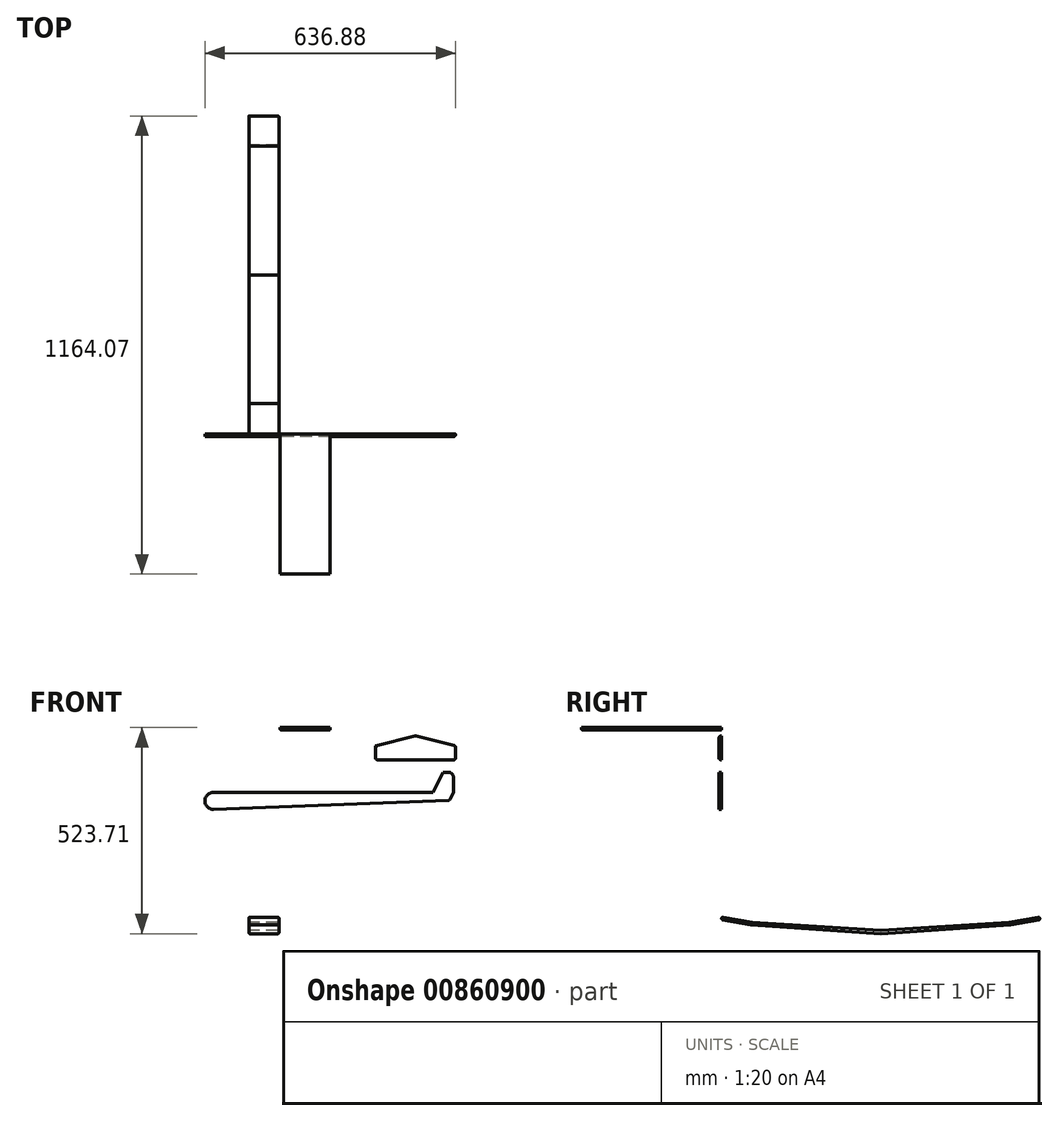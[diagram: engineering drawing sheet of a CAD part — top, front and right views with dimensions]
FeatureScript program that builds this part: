
annotation { "Feature Type Name" : "Feature", "Feature Type Description" : "" }
export const myFeature = defineFeature(function(context is Context, id is Id, definition is map)
    precondition{}
    {
        {
            var Q0;
            Q0=qCreatedBy(makeId("Front.planeOp"),FACE);
            var sketch = newSketch(context, id + "F0", { "sketchPlane" : qUnion([Q0])});
            skLineSegment(sketch, "E0", {"start": v(-90.11, 35.67) * mm, "end": v(445.18, 35.67) * mm});
            skLineSegment(sketch, "E1", {"start": v(493.61, 86.9) * mm, "end": v(506.79, 86.9) * mm});
            skLineSegment(sketch, "E2", {"start": v(519.49, 74.2) * mm, "end": v(519.49, 35.67) * mm});
            skPoint(sketch, "E3.orphan", {"position": v(468.96, 35.67) * mm});
            skLineSegment(sketch, "E4", {"start": v(467.72, 35.67) * mm, "end": v(445.18, 35.67) * mm});
            skLineSegment(sketch, "E5", {"start": v(493.61, 86.9) * mm, "end": v(467.72, 35.67) * mm});
            skPoint(sketch, "E6.visualSharp", {"position": v(519.49, 86.9) * mm});
            skArc(sketch, "E6.filletArc", {"start": v(519.49, 74.2) * mm, "mid": v(515.77, 83.19) * mm, "end": v(506.79, 86.9) * mm});
            skArc(sketch, "E7", {"start": v(-90.11, 35.67) * mm, "mid": v(-111.77, 14.01) * mm, "end": v(-90.11, -7.65) * mm});
            skLineSegment(sketch, "E8", {"start": v(-90.11, -7.65) * mm, "end": v(509.73, 15.45) * mm});
            skLineSegment(sketch, "E9", {"start": v(509.73, 15.45) * mm, "end": v(519.49, 35.67) * mm});
            skSolve(sketch);
        }
        {
            var Q0;
            Q0=qCreatedBy(makeId("Front.planeOp"),FACE);
            var sketch = newSketch(context, id + "F1", { "sketchPlane" : qUnion([Q0])});
            skLineSegment(sketch, "E10", {"start": v(321.9, 118.2) * mm, "end": v(321.9, 153.75) * mm});
            skLineSegment(sketch, "E11", {"start": v(321.9, 153.75) * mm, "end": v(423.5, 179.15) * mm});
            skLineSegment(sketch, "E12", {"start": v(423.5, 179.15) * mm, "end": v(423.5, 118.2) * mm});
            skLineSegment(sketch, "E13", {"start": v(423.5, 118.2) * mm, "end": v(321.9, 118.2) * mm});
            skLineSegment(sketch, "E14.MirrorCS", {"start": v(525.1, 153.75) * mm, "end": v(423.5, 179.15) * mm});
            skLineSegment(sketch, "E15.MirrorCS", {"start": v(423.5, 118.2) * mm, "end": v(525.1, 118.2) * mm});
            skLineSegment(sketch, "E16.MirrorCS", {"start": v(525.1, 118.2) * mm, "end": v(525.1, 153.75) * mm});
            skSolve(sketch);
        }
        {
            var Q0;
            Q0=qCreatedBy(makeId("Front.planeOp"),FACE);
            var sketch = newSketch(context, id + "F2", { "sketchPlane" : qUnion([Q0])});
            skLineSegment(sketch, "E17", {"start": v(79.4, 194.15) * mm, "end": v(206.4, 194.15) * mm});
            skLineSegment(sketch, "E18", {"start": v(206.4, 194.15) * mm, "end": v(206.4, 200.5) * mm});
            skLineSegment(sketch, "E19", {"start": v(206.4, 200.5) * mm, "end": v(79.4, 200.5) * mm});
            skLineSegment(sketch, "E20", {"start": v(79.4, 200.5) * mm, "end": v(79.4, 194.15) * mm});
            skSolve(sketch);
        }
        {
            var Q0;
            Q0=makeQuery(id+"F0.imprint","IMPRINT",FACE,{"disambiguationData":[TD([[makeQuery(id+"F0.imprint","IMPRINT",EDGE,{"derivedFrom":sQuery(id+"F0.wireOp",EDGE,"E0")}),-1.0]])]});
            extrude(context, id + "F3", {"entities" : qUnion([Q0]), "depth" : 6.35 * mm, "offsetDistance" : 25.4 * mm});
        }
        {
            var Q0;
            Q0=makeQuery(id+"F2.imprint","IMPRINT",FACE,{"disambiguationData":[TD([[makeQuery(id+"F2.imprint","IMPRINT",EDGE,{"derivedFrom":sQuery(id+"F2.wireOp",EDGE,"E17")}),1.0]])]});
            extrude(context, id + "F4", {"entities" : qUnion([Q0]), "depth" : 355.6 * mm, "offsetDistance" : 25.4 * mm});
        }
        {
            var Q0;
            Q0=makeQuery(id+"F4.opExtrude","SWEPT_EDGE",EDGE,{"disambiguationData":[OSD([sQuery(id+"F2.wireOp",EDGE,"E17"),sQuery(id+"F2.wireOp",EDGE,"E18")])]});
            var Q1;
            Q1=makeQuery(id+"F4.opExtrude","SWEPT_EDGE",EDGE,{"disambiguationData":[OSD([sQuery(id+"F2.wireOp",EDGE,"E17"),sQuery(id+"F2.wireOp",EDGE,"E20")])]});
            var Q2;
            Q2=makeQuery(id+"F4.opExtrude","CAP_EDGE",EDGE,{"disambiguationData":[OSD([sQuery(id+"F2.wireOp",EDGE,"E17")])],"isStart":false});
            var Q3;
            Q3=makeQuery(id+"F4.opExtrude","CAP_EDGE",EDGE,{"disambiguationData":[OSD([sQuery(id+"F2.wireOp",EDGE,"E17")])],"isStart":true});
            fillet(context, id + "F5", {"entities" : qUnion([Q0, Q1, Q2, Q3]), "radius" : 2.54 * mm, "tangentPropagation" : true, "allowEdgeOverflow" : false});
        }
        {
            var Q0;
            Q0=makeQuery(id+"F1.imprint","IMPRINT",FACE,{"disambiguationData":[TD([[makeQuery(id+"F1.imprint","IMPRINT",EDGE,{"derivedFrom":sQuery(id+"F1.wireOp",EDGE,"E10")}),-1.0]])]});
            var Q1;
            Q1=makeQuery(id+"F1.imprint","IMPRINT",FACE,{"disambiguationData":[TD([[makeQuery(id+"F1.imprint","IMPRINT",EDGE,{"derivedFrom":sQuery(id+"F1.wireOp",EDGE,"E12")}),1.0]])]});
            extrude(context, id + "F6", {"entities" : qUnion([Q0, Q1]), "depth" : 6.35 * mm, "offsetDistance" : 25.4 * mm});
        }
        {
            var Q0;
            Q0=qCreatedBy(makeId("Right.planeOp"),FACE);
            var sketch = newSketch(context, id + "F7", { "sketchPlane" : qUnion([Q0])});
            skLineSegment(sketch, "E21", {"start": v(404.44, -323.21) * mm, "end": v(75, -300.8) * mm});
            skLineSegment(sketch, "E22", {"start": v(75, -300.8) * mm, "end": v(0, -287.34) * mm});
            skLineSegment(sketch, "E23", {"start": v(0, -287.34) * mm, "end": v(1.12, -281.1) * mm});
            skLineSegment(sketch, "E24", {"start": v(1.12, -281.1) * mm, "end": v(77.4, -294.77) * mm});
            skLineSegment(sketch, "E25", {"start": v(77.4, -294.77) * mm, "end": v(404.44, -314.39) * mm});
            skLineSegment(sketch, "E26", {"start": v(404.44, -314.39) * mm, "end": v(404.44, -323.21) * mm});
            skLineSegment(sketch, "E27.MirrorCS", {"start": v(731.49, -294.77) * mm, "end": v(404.44, -314.39) * mm});
            skLineSegment(sketch, "E28.MirrorCS", {"start": v(807.76, -281.1) * mm, "end": v(731.49, -294.77) * mm});
            skLineSegment(sketch, "E29.MirrorCS", {"start": v(808.88, -287.34) * mm, "end": v(807.76, -281.1) * mm});
            skLineSegment(sketch, "E30.MirrorCS", {"start": v(733.88, -300.8) * mm, "end": v(808.88, -287.34) * mm});
            skLineSegment(sketch, "E31.MirrorCS", {"start": v(404.44, -323.21) * mm, "end": v(733.88, -300.8) * mm});
            skSolve(sketch);
        }
        {
            var Q0;
            Q0 = qSketchRegion(id + "F7", true);
            extrude(context, id + "F8", {"entities" : qUnion([Q0]), "depth" : 76.2 * mm, "offsetDistance" : 25.4 * mm});
        }
        {
            var Q0;
            Q0=makeQuery(id+"F8.opExtrude","SWEPT_EDGE",EDGE,{"disambiguationData":[OSD([sQuery(id+"F7.wireOp",EDGE,"E28.MirrorCS"),sQuery(id+"F7.wireOp",EDGE,"E29.MirrorCS")])]});
            var Q1;
            Q1=makeQuery(id+"F8.opExtrude","CAP_EDGE",EDGE,{"disambiguationData":[OSD([sQuery(id+"F7.wireOp",EDGE,"E28.MirrorCS")])],"isStart":false});
            var Q2;
            Q2=makeQuery(id+"F8.opExtrude","CAP_EDGE",EDGE,{"disambiguationData":[OSD([sQuery(id+"F7.wireOp",EDGE,"E27.MirrorCS")])],"isStart":false});
            var Q3;
            Q3=makeQuery(id+"F8.opExtrude","CAP_EDGE",EDGE,{"disambiguationData":[OSD([sQuery(id+"F7.wireOp",EDGE,"E25")])],"isStart":false});
            var Q4;
            Q4=makeQuery(id+"F8.opExtrude","SWEPT_EDGE",EDGE,{"disambiguationData":[OSD([sQuery(id+"F7.wireOp",EDGE,"E29.MirrorCS"),sQuery(id+"F7.wireOp",EDGE,"E30.MirrorCS")])]});
            var Q5;
            Q5=makeQuery(id+"F8.opExtrude","CAP_EDGE",EDGE,{"disambiguationData":[OSD([sQuery(id+"F7.wireOp",EDGE,"E30.MirrorCS")])],"isStart":false});
            var Q6;
            Q6=makeQuery(id+"F8.opExtrude","CAP_EDGE",EDGE,{"disambiguationData":[OSD([sQuery(id+"F7.wireOp",EDGE,"E29.MirrorCS")])],"isStart":false});
            var Q7;
            Q7=makeQuery(id+"F8.opExtrude","CAP_EDGE",EDGE,{"disambiguationData":[OSD([sQuery(id+"F7.wireOp",EDGE,"E31.MirrorCS")])],"isStart":false});
            var Q8;
            Q8=makeQuery(id+"F8.opExtrude","CAP_EDGE",EDGE,{"disambiguationData":[OSD([sQuery(id+"F7.wireOp",EDGE,"E21")])],"isStart":false});
            var Q9;
            Q9=makeQuery(id+"F8.opExtrude","CAP_EDGE",EDGE,{"disambiguationData":[OSD([sQuery(id+"F7.wireOp",EDGE,"E22")])],"isStart":false});
            var Q10;
            Q10=makeQuery(id+"F8.opExtrude","CAP_EDGE",EDGE,{"disambiguationData":[OSD([sQuery(id+"F7.wireOp",EDGE,"E24")])],"isStart":false});
            var Q11;
            Q11=makeQuery(id+"F8.opExtrude","CAP_EDGE",EDGE,{"disambiguationData":[OSD([sQuery(id+"F7.wireOp",EDGE,"E23")])],"isStart":false});
            var Q12;
            Q12=makeQuery(id+"F8.opExtrude","SWEPT_EDGE",EDGE,{"disambiguationData":[OSD([sQuery(id+"F7.wireOp",EDGE,"E23"),sQuery(id+"F7.wireOp",EDGE,"E24")])]});
            var Q13;
            Q13=makeQuery(id+"F8.opExtrude","CAP_EDGE",EDGE,{"disambiguationData":[OSD([sQuery(id+"F7.wireOp",EDGE,"E23")])],"isStart":true});
            var Q14;
            Q14=makeQuery(id+"F8.opExtrude","SWEPT_EDGE",EDGE,{"disambiguationData":[OSD([sQuery(id+"F7.wireOp",EDGE,"E22"),sQuery(id+"F7.wireOp",EDGE,"E23")])]});
            var Q15;
            Q15=makeQuery(id+"F8.opExtrude","CAP_EDGE",EDGE,{"disambiguationData":[OSD([sQuery(id+"F7.wireOp",EDGE,"E27.MirrorCS")])],"isStart":true});
            var Q16;
            Q16=makeQuery(id+"F8.opExtrude","CAP_EDGE",EDGE,{"disambiguationData":[OSD([sQuery(id+"F7.wireOp",EDGE,"E31.MirrorCS")])],"isStart":true});
            var Q17;
            Q17=makeQuery(id+"F8.opExtrude","CAP_EDGE",EDGE,{"disambiguationData":[OSD([sQuery(id+"F7.wireOp",EDGE,"E21")])],"isStart":true});
            var Q18;
            Q18=makeQuery(id+"F8.opExtrude","CAP_EDGE",EDGE,{"disambiguationData":[OSD([sQuery(id+"F7.wireOp",EDGE,"E25")])],"isStart":true});
            var Q19;
            Q19=makeQuery(id+"F8.opExtrude","CAP_EDGE",EDGE,{"disambiguationData":[OSD([sQuery(id+"F7.wireOp",EDGE,"E24")])],"isStart":true});
            var Q20;
            Q20=makeQuery(id+"F8.opExtrude","CAP_EDGE",EDGE,{"disambiguationData":[OSD([sQuery(id+"F7.wireOp",EDGE,"E22")])],"isStart":true});
            var Q21;
            Q21=makeQuery(id+"F8.opExtrude","CAP_EDGE",EDGE,{"disambiguationData":[OSD([sQuery(id+"F7.wireOp",EDGE,"E30.MirrorCS")])],"isStart":true});
            var Q22;
            Q22=makeQuery(id+"F8.opExtrude","CAP_EDGE",EDGE,{"disambiguationData":[OSD([sQuery(id+"F7.wireOp",EDGE,"E28.MirrorCS")])],"isStart":true});
            fillet(context, id + "F9", {"entities" : qUnion([Q0, Q1, Q2, Q3, Q4, Q5, Q6, Q7, Q8, Q9, Q10, Q11, Q12, Q13, Q14, Q15, Q16, Q17, Q18, Q19, Q20, Q21, Q22]), "radius" : 2.54 * mm, "tangentPropagation" : true, "allowEdgeOverflow" : false});
        }
        {
            var Q0;
            Q0=makeQuery(id+"F6.opExtrude","CAP_EDGE",EDGE,{"disambiguationData":[OSD([sQuery(id+"F1.wireOp",EDGE,"E16.MirrorCS")])],"isStart":false});
            var Q1;
            Q1=makeQuery(id+"F6.opExtrude","CAP_EDGE",EDGE,{"disambiguationData":[OSD([sQuery(id+"F1.wireOp",EDGE,"E11")])],"isStart":false});
            var Q2;
            Q2=makeQuery(id+"F6.opExtrude","SWEPT_EDGE",EDGE,{"disambiguationData":[OSD([sQuery(id+"F1.wireOp",EDGE,"E11"),sQuery(id+"F1.wireOp",EDGE,"E12"),sQuery(id+"F1.wireOp",EDGE,"E14.MirrorCS")])]});
            var Q3;
            Q3=makeQuery(id+"F6.opExtrude","CAP_EDGE",EDGE,{"disambiguationData":[OSD([sQuery(id+"F1.wireOp",EDGE,"E14.MirrorCS")])],"isStart":false});
            var Q4;
            Q4=makeQuery(id+"F3.opExtrude","SWEPT_EDGE",EDGE,{"disambiguationData":[OSD([sQuery(id+"F0.wireOp",EDGE,"E8"),sQuery(id+"F0.wireOp",EDGE,"E9")])]});
            var Q5;
            Q5=makeQuery(id+"F6.opExtrude","CAP_EDGE",EDGE,{"disambiguationData":[OSD([sQuery(id+"F1.wireOp",EDGE,"E13"),sQuery(id+"F1.wireOp",EDGE,"E15.MirrorCS")])],"isStart":false});
            var Q6;
            Q6=makeQuery(id+"F6.opExtrude","CAP_EDGE",EDGE,{"disambiguationData":[OSD([sQuery(id+"F1.wireOp",EDGE,"E10")])],"isStart":false});
            var Q7;
            Q7=makeQuery(id+"F6.opExtrude","SWEPT_EDGE",EDGE,{"disambiguationData":[OSD([sQuery(id+"F1.wireOp",EDGE,"E10"),sQuery(id+"F1.wireOp",EDGE,"E13")])]});
            var Q8;
            Q8=makeQuery(id+"F6.opExtrude","SWEPT_EDGE",EDGE,{"disambiguationData":[OSD([sQuery(id+"F1.wireOp",EDGE,"E15.MirrorCS"),sQuery(id+"F1.wireOp",EDGE,"E16.MirrorCS")])]});
            var Q9;
            Q9=makeQuery(id+"F6.opExtrude","SWEPT_EDGE",EDGE,{"disambiguationData":[OSD([sQuery(id+"F1.wireOp",EDGE,"E14.MirrorCS"),sQuery(id+"F1.wireOp",EDGE,"E16.MirrorCS")])]});
            fillet(context, id + "F10", {"entities" : qUnion([Q0, Q1, Q2, Q3, Q4, Q5, Q6, Q7, Q8, Q9]), "radius" : 5.08 * mm, "tangentPropagation" : true, "allowEdgeOverflow" : false});
        }
    });
